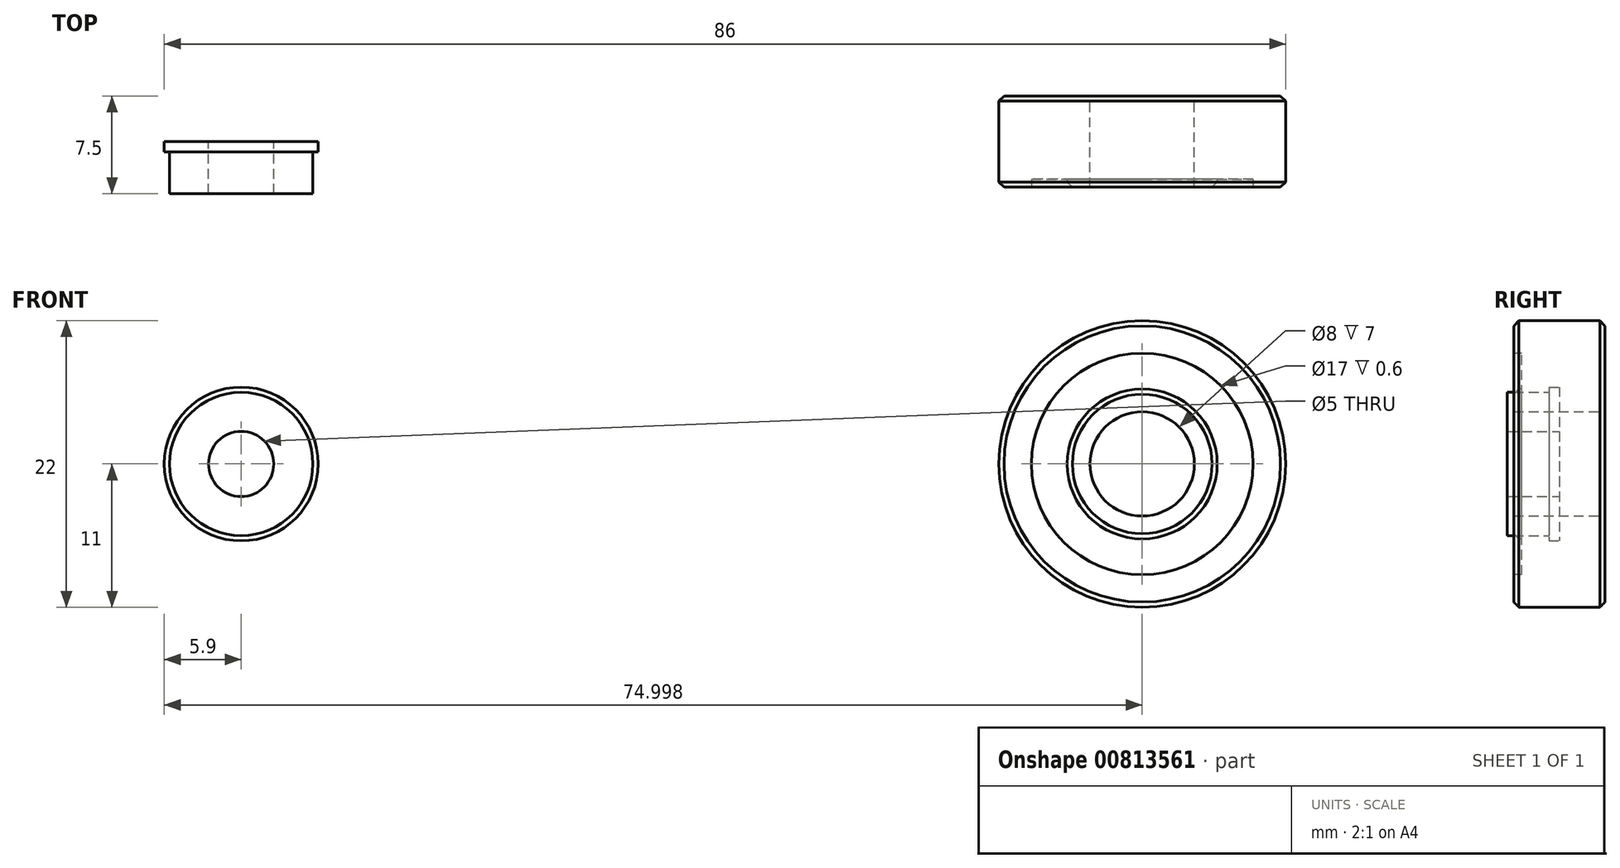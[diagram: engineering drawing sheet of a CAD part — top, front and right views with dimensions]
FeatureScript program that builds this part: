
annotation { "Feature Type Name" : "Feature", "Feature Type Description" : "" }
export const myFeature = defineFeature(function(context is Context, id is Id, definition is map)
    precondition{}
    {
        {
            var Q0;
            Q0=qCreatedBy(makeId("Right.planeOp"),FACE);
            var sketch = newSketch(context, id + "F0", { "sketchPlane" : qUnion([Q0])});
            skLineSegment(sketch, "E0", {"start": v(3.3, 0) * mm, "end": v(-12.28, 0) * mm, "construction": true});
            skLineSegment(sketch, "E1", {"start": v(0, 5.9) * mm, "end": v(-0.8, 5.9) * mm});
            skLineSegment(sketch, "E2", {"start": v(-0.8, 5.9) * mm, "end": v(-0.8, 5.5) * mm});
            skLineSegment(sketch, "E3", {"start": v(-0.8, 5.5) * mm, "end": v(-4, 5.5) * mm});
            skLineSegment(sketch, "E4", {"start": v(-4, 5.5) * mm, "end": v(-4, 2.5) * mm});
            skLineSegment(sketch, "E5", {"start": v(-4, 2.5) * mm, "end": v(0, 2.5) * mm});
            skLineSegment(sketch, "E6", {"start": v(0, 2.5) * mm, "end": v(0, 5.9) * mm});
            skSolve(sketch);
        }
        {
            var Q0;
            Q0=qSketchRegion(id+"F0",true);
            var Q1;
            Q1=sQuery(id+"F0.wireOp",EDGE,"E0");
            revolve(context, id + "F1", {"surfaceOperationType" : NewSurfaceOperationType.NEW, "entities" : qUnion([Q0]), "axis" : qUnion([Q1]), "revolveType" : RevolveType.FULL});
        }
        {
            var Q0;
            Q0=qCreatedBy(makeId("Front.planeOp"),FACE);
            var sketch = newSketch(context, id + "F2", { "sketchPlane" : qUnion([Q0])});
            skCircle(sketch, "E7", {"center": v(35.4, 0) * mm, "radius": 4 * mm});
            skCircle(sketch, "E8", {"center": v(35.4, 0) * mm, "radius": 11 * mm});
            skSolve(sketch);
        }
        {
            var Q0;
            Q0=makeQuery(id+"F1.opRevolve","SWEPT_BODY",BODY,{"disambiguationData":[OSD([sQuery(id+"F0.wireOp",EDGE,"E1"),sQuery(id+"F0.wireOp",EDGE,"E2"),sQuery(id+"F0.wireOp",EDGE,"E3"),sQuery(id+"F0.wireOp",EDGE,"E4"),sQuery(id+"F0.wireOp",EDGE,"E5"),sQuery(id+"F0.wireOp",EDGE,"E6")])]});
            transform(context, id + "F3", {"entities" : qUnion([Q0]), "transformType" : TransformType.TRANSLATION_3D, "dx" : -33.7 * mm, "dy" : 0 * mm, "dz" : 0 * mm, "makeCopy" : false});
        }
        {
            var Q0;
            Q0=makeQuery(id+"F2.imprint","IMPRINT",FACE,{"disambiguationData":[TD([[makeQuery(id+"F2.imprint","IMPRINT",EDGE,{"derivedFrom":sQuery(id+"F2.wireOp",EDGE,"E7")}),-1.0]])]});
            extrude(context, id + "F4", {"entities" : qUnion([Q0]), "endBound" : BoundingType.SYMMETRIC, "depth" : 7 * mm, "offsetDistance" : 25 * mm});
        }
        {
            var Q0;
            Q0=makeQuery(id+"F4.opExtrude","CAP_FACE",FACE,{"disambiguationData":[OSD([sQuery(id+"F2.wireOp",EDGE,"E7"),sQuery(id+"F2.wireOp",EDGE,"E8")])],"isStart":false});
            var sketch = newSketch(context, id + "F5", { "sketchPlane" : qUnion([Q0])});
            skCircle(sketch, "E9", {"center": v(35.4, 0) * mm, "radius": 5.75 * mm});
            skCircle(sketch, "E10", {"center": v(35.4, 0) * mm, "radius": 8.5 * mm});
            skSolve(sketch);
        }
        {
            var Q0;
            Q0=makeQuery(id+"F5.imprint","IMPRINT",FACE,{"disambiguationData":[TD([[makeQuery(id+"F5.imprint","IMPRINT",EDGE,{"derivedFrom":sQuery(id+"F5.wireOp",EDGE,"E9")}),-1.0]])]});
            extrude(context, id + "F6", {"entities" : qUnion([Q0]), "operationType" : NewBodyOperationType.REMOVE, "oppositeDirection" : true, "depth" : 0.6 * mm, "offsetDistance" : 25 * mm});
        }
        {
            var Q0;
            Q0=makeQuery(id+"F4.opExtrude","CAP_EDGE",EDGE,{"disambiguationData":[OSD([sQuery(id+"F2.wireOp",EDGE,"E8")])],"isStart":false});
            var Q1;
            Q1=makeQuery(id+"F6.boolean.opBoolean","COPY",EDGE,{"derivedFrom":makeQuery(id+"F6.opExtrude","CAP_EDGE",EDGE,{"disambiguationData":[OSD([sQuery(id+"F5.wireOp",EDGE,"E10")])],"isStart":true})});
            var Q2;
            Q2=makeQuery(id+"F6.boolean.opBoolean","COPY",EDGE,{"derivedFrom":makeQuery(id+"F6.opExtrude","CAP_EDGE",EDGE,{"disambiguationData":[OSD([sQuery(id+"F5.wireOp",EDGE,"E9")])],"isStart":true})});
            var Q3;
            Q3=makeQuery(id+"FAqd1R1ERXR4cZm_4.1.F6.boolean.opBoolean","COPY",EDGE,{"derivedFrom":makeQuery(id+"FAqd1R1ERXR4cZm_4.1.F6.opExtrude","CAP_EDGE",EDGE,{"disambiguationData":[OSD([sQuery(id+"F5.wireOp",EDGE,"E9")])],"isStart":true})});
            var Q4;
            Q4=makeQuery(id+"FAqd1R1ERXR4cZm_4.1.F6.boolean.opBoolean","COPY",EDGE,{"derivedFrom":makeQuery(id+"FAqd1R1ERXR4cZm_4.1.F6.opExtrude","CAP_EDGE",EDGE,{"disambiguationData":[OSD([sQuery(id+"F5.wireOp",EDGE,"E10")])],"isStart":true})});
            var Q5;
            Q5=makeQuery(id+"F4.opExtrude","CAP_EDGE",EDGE,{"disambiguationData":[OSD([sQuery(id+"F2.wireOp",EDGE,"E8")])],"isStart":true});
            chamfer(context, id + "F7", {"entities" : qUnion([Q0, Q1, Q2, Q3, Q4, Q5]), "width" : 0.4 * mm, "tangentPropagation" : true});
        }
    });
